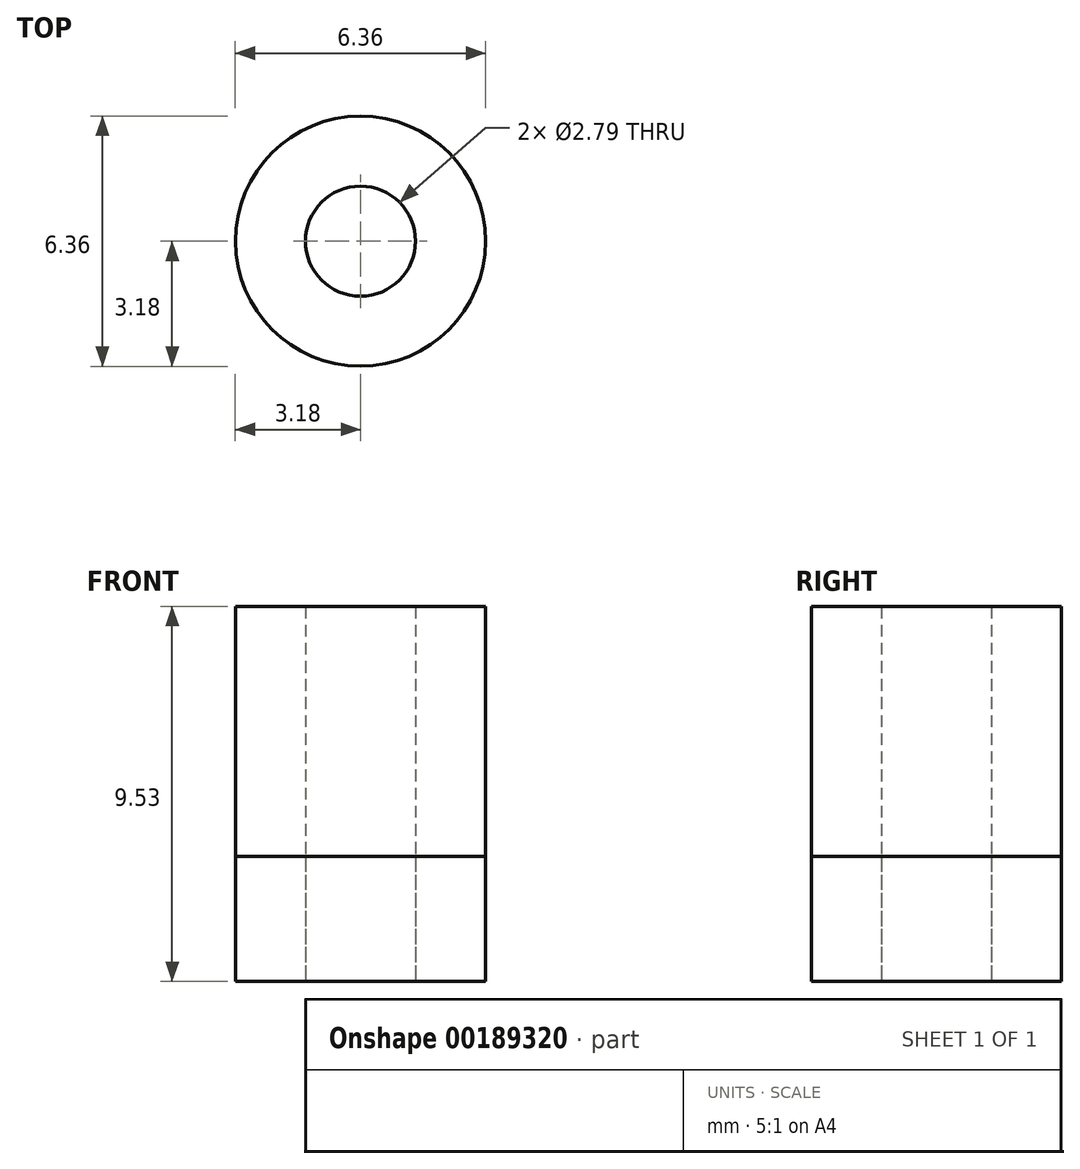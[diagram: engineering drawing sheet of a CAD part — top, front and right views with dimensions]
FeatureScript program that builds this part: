
annotation { "Feature Type Name" : "Feature", "Feature Type Description" : "" }
export const myFeature = defineFeature(function(context is Context, id is Id, definition is map)
    precondition{}
    {
        {
            var Q0;
            Q0=qCreatedBy(makeId("Top.planeOp"),FACE);
            var sketch = newSketch(context, id + "F0", { "sketchPlane" : qUnion([Q0])});
            skCircle(sketch, "E0", {"center": v(0, 0) * mm, "radius": 1.4 * mm});
            skCircle(sketch, "E1", {"center": v(0, 0) * mm, "radius": 3.18 * mm});
            skSolve(sketch);
        }
        {
            var Q0;
            Q0=makeQuery(id+"F0.imprint","IMPRINT",FACE,{"disambiguationData":[TD([[makeQuery(id+"F0.imprint","IMPRINT",EDGE,{"derivedFrom":sQuery(id+"F0.wireOp",EDGE,"E0")}),-1.0]])]});
            extrude(context, id + "F1", {"entities" : qUnion([Q0]), "depth" : 9.52 * mm});
        }
        {
            var Q0;
            Q0=makeQuery(id+"F1.opExtrude","CAP_FACE",FACE,{"disambiguationData":[OSD([sQuery(id+"F0.wireOp",EDGE,"E0"),sQuery(id+"F0.wireOp",EDGE,"E1")])],"isStart":true});
            extrude(context, id + "F2", {"entities" : qUnion([Q0]), "oppositeDirection" : true, "depth" : 3.17 * mm});
        }
    });
